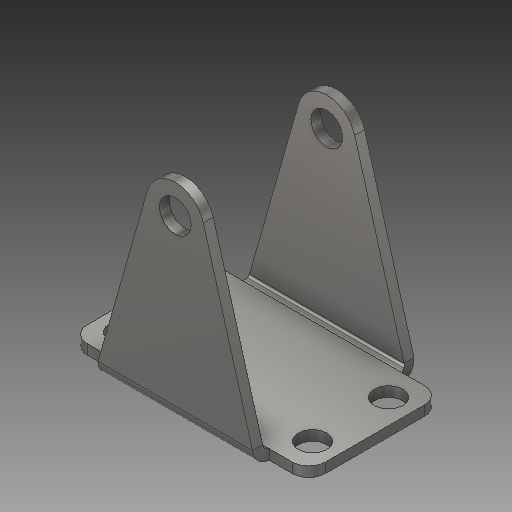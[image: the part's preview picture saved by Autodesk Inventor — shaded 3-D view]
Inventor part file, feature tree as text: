
AUTODESK INVENTOR PART (.ipt)
format: ipt  version: 2018 (Build 220112000, 112)  size: 212,480 bytes
history: native  units: in
note: dims shown in document units (in); Inventor stores cm internally (conversion verified against a paired STEP export)
features: sketch x4, extrude x2, other x2
ambient origin geometry x8: Origin, YZ Plane, XZ Plane, XY Plane, X Axis, Y Axis, Z Axis, Center Point
bodies: Solid1 (feature_tree)
feature tree (8):
  extrude  "Extrusion1"  Depth=1.0in
  extrude  "Extrusion2"  Depth=0.125in
  other  "Bend Part1"
  other  "Bend Part2"
  sketch  "Sketch1"  dims[d0=1.8in d1=1.0in]
  sketch  "Sketch3"  dims[d2=0.075in d3=0.0in d4=0.125in]
  sketch  "Sketch4"  dims[d5=1.43in]
  sketch  "Sketch5"  dims[d6=0.575in d7=0.215in d8=0.215in d9=0.215in d10=0.215in d11=0.6in d12=0.0in d16=1.3in d17=0.6in d18=0.6in d19=0.0in d20=0.22in d21=0.075in d22=0.0in d23=0.24in d24=0.035in d25=90.0deg d26=0.035in d27=90.0deg]
